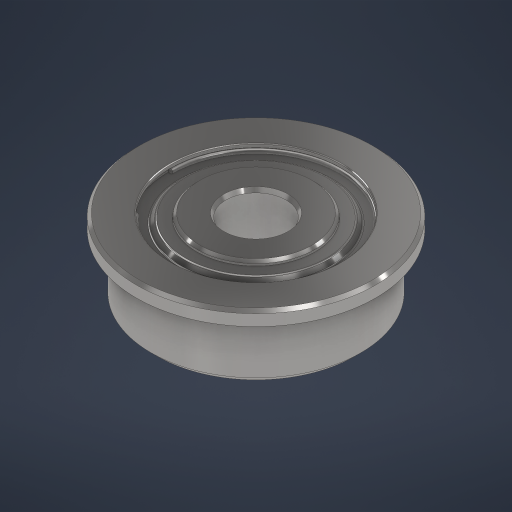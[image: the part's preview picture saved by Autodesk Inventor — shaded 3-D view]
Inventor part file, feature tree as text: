
AUTODESK INVENTOR PART (.ipt)
format: ipt  version: 2024 (Build 280153000, 153)  size: 351,232 bytes
history: native  units: in
note: dims shown in document units (in); Inventor stores cm internally (conversion verified against a paired STEP export)
features: revolve x1, mirror x1, chamfer x1
ambient origin geometry x8: Origin, YZ Plane, XZ Plane, XY Plane, X Axis, Y Axis, Z Axis, Center Point
bodies: Solid1 (feature_tree), Solid2 (feature_tree), Solid3 (feature_tree)
feature tree (3):
  revolve  "Revolve1"  [1 undecoded]
  mirror  "Mirror3"
  chamfer  "Chamfer7"  [1 undecoded]
note: 2 required parameter values undecoded (feature->parameter linkage not recoverable at this tier; creation-order binding heuristic only, values carry confidence <= 0.55)
